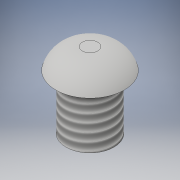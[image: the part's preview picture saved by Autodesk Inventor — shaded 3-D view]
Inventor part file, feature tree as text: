
AUTODESK INVENTOR PART (.ipt)
format: ipt  version: 2019.1 (Build 231200000, 200)  size: 128,000 bytes
history: native  units: in
note: dims shown in document units (in); Inventor stores cm internally (conversion verified against a paired STEP export)
features: extrude x2, sketch x2, thread x1, fillet x1
ambient origin geometry x8: Origin, YZ Plane, XZ Plane, XY Plane, X Axis, Y Axis, Z Axis, Center Point
bodies: Solid1 (feature_tree)
feature tree (6):
  extrude  "Extrusion1"  Depth=0.1575in TaperAngle=0.0deg
  thread  "Thread1"  [1 undecoded]
  extrude  "Extrusion2"  Depth=0.0591in TaperAngle=0.0deg
  fillet  "Fillet1"  Radius=0.0787in
  sketch  "Sketch1"  dims[d0=0.1378in d1=0.1575in d2=0.0in d3=0.3937in d4=0.0in]
  sketch  "Sketch2"  dims[d5=0.1969in d6=0.0591in d7=0.0in d8=0.0787in]
note: 1 required parameter value undecoded (feature->parameter linkage not recoverable at this tier; creation-order binding heuristic only, values carry confidence <= 0.55)
